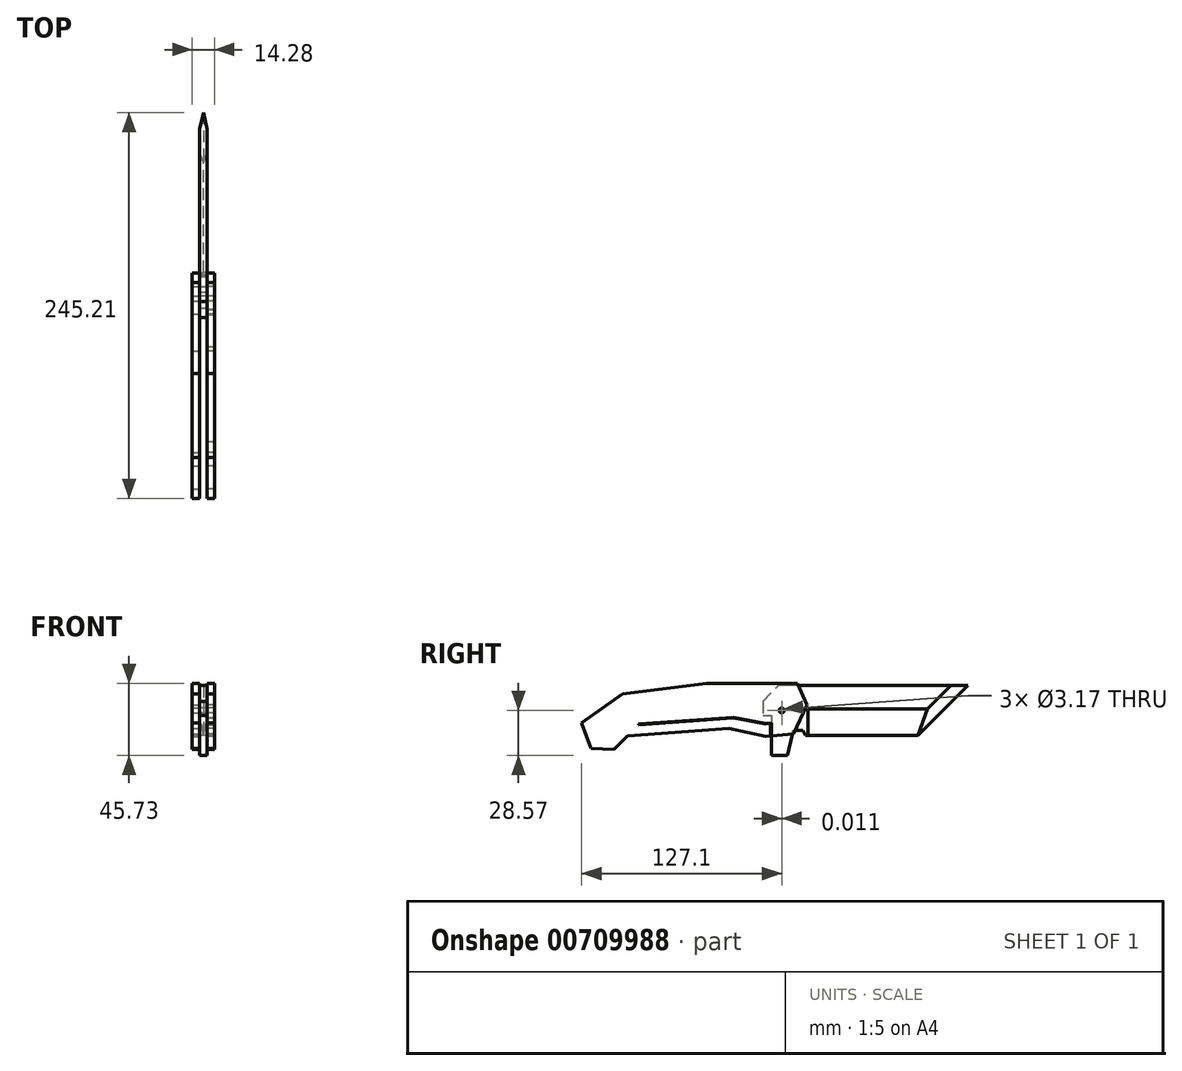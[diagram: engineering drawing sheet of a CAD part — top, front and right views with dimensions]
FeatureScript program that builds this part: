
annotation { "Feature Type Name" : "Feature", "Feature Type Description" : "" }
export const myFeature = defineFeature(function(context is Context, id is Id, definition is map)
    precondition{}
    {
        {
            var Q0;
            Q0=qCreatedBy(makeId("Right.planeOp"),FACE);
            var sketch = newSketch(context, id + "F0", { "sketchPlane" : qUnion([Q0])});
            skLineSegment(sketch, "E0.bottom", {"start": v(50.8, 15.88) * mm, "end": v(-50.8, 15.88) * mm});
            skLineSegment(sketch, "E0.top", {"start": v(50.8, -15.88) * mm, "end": v(-50.8, -15.88) * mm});
            skLineSegment(sketch, "E0.left", {"start": v(50.8, 15.88) * mm, "end": v(50.8, -15.88) * mm});
            skLineSegment(sketch, "E0.right", {"start": v(-50.8, 15.88) * mm, "end": v(-50.8, -15.88) * mm});
            skPoint(sketch, "E0.middle", {"position": v(0, 0) * mm});
            skSolve(sketch);
        }
        {
            var Q0;
            Q0 = qSketchRegion(id + "F0", true);
            extrude(context, id + "F1", {"entities" : qUnion([Q0]), "endBound" : BoundingType.SYMMETRIC, "oppositeDirection" : true, "depth" : 4.76 * mm, "offsetDistance" : 25.4 * mm});
        }
        {
            var Q0;
            Q0=makeQuery(id+"F1.opExtrude","SWEPT_FACE",FACE,{"disambiguationData":[OSD([sQuery(id+"F0.wireOp",EDGE,"E0.left")])]});
            var sketch = newSketch(context, id + "F2", { "sketchPlane" : qUnion([Q0])});
            skLineSegment(sketch, "E1", {"start": v(0, -15.87) * mm, "end": v(-2.38, 1.07) * mm});
            skLineSegment(sketch, "E2", {"start": v(0, -15.87) * mm, "end": v(0, -2.24) * mm, "construction": true});
            skLineSegment(sketch, "E3", {"start": v(0, -15.88) * mm, "end": v(2.38, 1.07) * mm});
            skLineSegment(sketch, "E4", {"start": v(-2.38, 1.07) * mm, "end": v(-18.49, 1.07) * mm});
            skLineSegment(sketch, "E5", {"start": v(-18.49, 1.07) * mm, "end": v(-18.49, -23.62) * mm});
            skLineSegment(sketch, "E6", {"start": v(-18.49, -23.62) * mm, "end": v(17.54, -23.62) * mm});
            skLineSegment(sketch, "E7", {"start": v(17.54, -23.62) * mm, "end": v(17.54, 1.07) * mm});
            skLineSegment(sketch, "E8", {"start": v(17.54, 1.07) * mm, "end": v(2.38, 1.07) * mm});
            skSolve(sketch);
        }
        {
            var Q0;
            Q0 = qSketchRegion(id + "F2", true);
            extrude(context, id + "F3", {"entities" : qUnion([Q0]), "operationType" : NewBodyOperationType.REMOVE, "endBound" : BoundingType.THROUGH_ALL, "oppositeDirection" : true, "depth" : 25.4 * mm, "offsetDistance" : 25.4 * mm});
        }
        {
            var Q0;
            Q0=qCreatedBy(makeId("Right.planeOp"),FACE);
            var sketch = newSketch(context, id + "F4", { "sketchPlane" : qUnion([Q0])});
            skLineSegment(sketch, "E9", {"start": v(50.8, 15.88) * mm, "end": v(19.05, -15.88) * mm});
            skSolve(sketch);
        }
        {
            var Q0;
            Q0=makeQuery(id+"F1.opExtrude","SWEPT_FACE",FACE,{"disambiguationData":[OSD([sQuery(id+"F0.wireOp",EDGE,"E0.bottom")])]});
            var sketch = newSketch(context, id + "F5", { "sketchPlane" : qUnion([Q0])});
            skLineSegment(sketch, "E10", {"start": v(0, 50.8) * mm, "end": v(2.38, 40.06) * mm});
            skLineSegment(sketch, "E11", {"start": v(0, 50.8) * mm, "end": v(-2.38, 40.06) * mm});
            skLineSegment(sketch, "E12", {"start": v(2.38, 40.06) * mm, "end": v(25.29, 40.06) * mm});
            skLineSegment(sketch, "E13", {"start": v(25.29, 40.06) * mm, "end": v(21.97, 103.42) * mm});
            skLineSegment(sketch, "E14", {"start": v(21.97, 103.42) * mm, "end": v(-23.8, 103.42) * mm});
            skLineSegment(sketch, "E15", {"start": v(-23.8, 103.42) * mm, "end": v(-27.67, 37.97) * mm});
            skLineSegment(sketch, "E16", {"start": v(-27.67, 37.97) * mm, "end": v(-2.38, 40.06) * mm});
            skSolve(sketch);
        }
        {
            var Q0;
            Q0 = qSketchRegion(id + "F5", true);
            var Q1;
            Q1 = qSketchRegion(id + "F4", true);
            var Q2;
            Q2 = qConstructionFilter(qBodyType(qCreatedBy(id + "F4" ,EDGE), BodyType.WIRE), ConstructionObject.NO);
            sweep(context, id + "F6", {"operationType" : NewBodyOperationType.REMOVE, "profiles" : qUnion([Q0, Q1]), "path" : qUnion([Q2])});
        }
        {
            var Q0;
            Q0=qCreatedBy(makeId("Right.planeOp"),FACE);
            var sketch = newSketch(context, id + "F7", { "sketchPlane" : qUnion([Q0])});
            skLineSegment(sketch, "E17", {"start": v(-50.8, -15.87) * mm, "end": v(-52.39, -15.87) * mm});
            skLineSegment(sketch, "E18", {"start": v(-50.8, 15.88) * mm, "end": v(-79.38, 15.87) * mm});
            skLineSegment(sketch, "E19", {"start": v(-79.38, 15.87) * mm, "end": v(-79.38, -3.17) * mm});
            skLineSegment(sketch, "E20", {"start": v(-79.38, -3.18) * mm, "end": v(-73.85, -3.18) * mm});
            skLineSegment(sketch, "E21", {"start": v(-73.85, -3.18) * mm, "end": v(-73.85, -28.58) * mm});
            skLineSegment(sketch, "E22", {"start": v(-73.85, -28.58) * mm, "end": v(-63.69, -28.58) * mm});
            skLineSegment(sketch, "E23", {"start": v(-63.69, -28.58) * mm, "end": v(-60.04, -12.7) * mm});
            skLineSegment(sketch, "E24", {"start": v(-60.04, -12.7) * mm, "end": v(-53.69, -12.7) * mm});
            skLineSegment(sketch, "E25", {"start": v(-53.69, -12.7) * mm, "end": v(-52.39, -15.87) * mm});
            skLineSegment(sketch, "E26", {"start": v(-50.8, 15.88) * mm, "end": v(-50.8, -15.87) * mm});
            skCircle(sketch, "E27", {"center": v(-67.31, 0) * mm, "radius": 1.59 * mm});
            skSolve(sketch);
        }
        {
            var Q0;
            Q0 = qSketchRegion(id + "F7", true);
            extrude(context, id + "F8", {"entities" : qUnion([Q0]), "operationType" : NewBodyOperationType.ADD, "endBound" : BoundingType.SYMMETRIC, "depth" : 4.76 * mm, "offsetDistance" : 25.4 * mm});
        }
        {
            var Q0;
            Q0=makeQuery(id+"F8.opExtrude","SWEPT_EDGE",EDGE,{"disambiguationData":[OSD([sQuery(id+"F7.wireOp",EDGE,"E18"),sQuery(id+"F7.wireOp",EDGE,"E19")])]});
            chamfer(context, id + "F9", {"entities" : qUnion([Q0]), "width" : 10.16 * mm, "tangentPropagation" : true});
        }
        {
            var Q0;
            Q0=makeQuery(id+"F8.boolean.opBoolean","MERGE",FACE,{"derivedFrom":[makeQuery(id+"F1.opExtrude","CAP_FACE",FACE,{"disambiguationData":[OSD([sQuery(id+"F0.wireOp",EDGE,"E0.bottom"),sQuery(id+"F0.wireOp",EDGE,"E0.top"),sQuery(id+"F0.wireOp",EDGE,"E0.left"),sQuery(id+"F0.wireOp",EDGE,"E0.right")])],"isStart":true}),makeQuery(id+"F8.opExtrude","CAP_FACE",FACE,{"disambiguationData":[OSD([sQuery(id+"F7.wireOp",EDGE,"E17"),sQuery(id+"F7.wireOp",EDGE,"E18"),sQuery(id+"F7.wireOp",EDGE,"E19"),sQuery(id+"F7.wireOp",EDGE,"E20"),sQuery(id+"F7.wireOp",EDGE,"E21"),sQuery(id+"F7.wireOp",EDGE,"E22"),sQuery(id+"F7.wireOp",EDGE,"E23"),sQuery(id+"F7.wireOp",EDGE,"E24"),sQuery(id+"F7.wireOp",EDGE,"E25"),sQuery(id+"F7.wireOp",EDGE,"E26"),sQuery(id+"F7.wireOp",EDGE,"E27")])],"isStart":false})]});
            var sketch = newSketch(context, id + "F10", { "sketchPlane" : qUnion([Q0])});
            skCircle(sketch, "E28", {"center": v(-67.31, 0) * mm, "radius": 15.88 * mm, "construction": true});
            skSolve(sketch);
        }
        {
            var Q0;
            {var subQ8=sQuery(id+"F7.wireOp",EDGE,"E17");Q0=makeQuery(id+"F10.imprint","IMPRINT",FACE,{"disambiguationData":[TD([[makeQuery(id+"F10.imprint","IMPRINT",EDGE,{"derivedFrom":makeQuery(id+"F8.opExtrude","CAP_EDGE",EDGE,{"disambiguationData":[OSD([subQ8])],"isStart":false})}),-1.0]])]});}
            var sketch = newSketch(context, id + "F11", { "sketchPlane" : qUnion([Q0])});
            skLineSegment(sketch, "E29", {"start": v(-115.05, 17.16) * mm, "end": v(-57.22, 17.16) * mm});
            skLineSegment(sketch, "E30", {"start": v(-57.22, 17.16) * mm, "end": v(-51.23, 3.41) * mm});
            skLineSegment(sketch, "E31", {"start": v(-51.23, 3.41) * mm, "end": v(-59.74, -14.96) * mm});
            skLineSegment(sketch, "E32", {"start": v(-59.74, -14.96) * mm, "end": v(-77.17, -16.54) * mm});
            skLineSegment(sketch, "E33", {"start": v(-77.17, -16.54) * mm, "end": v(-100.87, -11.45) * mm});
            skLineSegment(sketch, "E34", {"start": v(-100.87, -11.45) * mm, "end": v(-165.33, -16.07) * mm});
            skPoint(sketch, "E34.endSnap0", {"position": v(-89.02, -14) * mm});
            skLineSegment(sketch, "E35", {"start": v(-165.33, -16.07) * mm, "end": v(-173.7, -24.81) * mm});
            skLineSegment(sketch, "E36", {"start": v(-188.34, -24.23) * mm, "end": v(-173.7, -24.81) * mm});
            skLineSegment(sketch, "E37", {"start": v(-188.34, -24.23) * mm, "end": v(-194.41, -8) * mm});
            skLineSegment(sketch, "E38", {"start": v(-194.41, -8) * mm, "end": v(-168.37, 10.54) * mm});
            skLineSegment(sketch, "E39", {"start": v(-168.37, 10.54) * mm, "end": v(-115.05, 17.16) * mm});
            skCircle(sketch, "E40", {"center": v(-67.3, 0) * mm, "radius": 1.59 * mm});
            skSolve(sketch);
        }
        {
            var Q0;
            Q0 = qSketchRegion(id + "F11", true);
            extrude(context, id + "F12", {"entities" : qUnion([Q0]), "depth" : 4.76 * mm, "offsetDistance" : 25.4 * mm});
        }
        {
            var Q0;
            Q0=makeQuery(id+"F12.opExtrude","SWEPT_BODY",BODY,{"disambiguationData":[OSD([sQuery(id+"F11.wireOp",EDGE,"E29"),sQuery(id+"F11.wireOp",EDGE,"E30"),sQuery(id+"F11.wireOp",EDGE,"E31"),sQuery(id+"F11.wireOp",EDGE,"E32"),sQuery(id+"F11.wireOp",EDGE,"E33"),sQuery(id+"F11.wireOp",EDGE,"E34"),sQuery(id+"F11.wireOp",EDGE,"E35"),sQuery(id+"F11.wireOp",EDGE,"E36"),sQuery(id+"F11.wireOp",EDGE,"E37"),sQuery(id+"F11.wireOp",EDGE,"E38"),sQuery(id+"F11.wireOp",EDGE,"E39"),sQuery(id+"F11.wireOp",EDGE,"E40")])]});
            var Q1;
            Q1=qCreatedBy(makeId("Right.planeOp"),FACE);
            mirror(context, id + "F13", {"entities" : qUnion([Q0]), "mirrorPlane" : qUnion([Q1])});
        }
        {
            var Q0;
            Q0=makeQuery(id+"F12.opExtrude","CAP_FACE",FACE,{"disambiguationData":[OSD([sQuery(id+"F11.wireOp",EDGE,"E29"),sQuery(id+"F11.wireOp",EDGE,"E30"),sQuery(id+"F11.wireOp",EDGE,"E31"),sQuery(id+"F11.wireOp",EDGE,"E32"),sQuery(id+"F11.wireOp",EDGE,"E33"),sQuery(id+"F11.wireOp",EDGE,"E34"),sQuery(id+"F11.wireOp",EDGE,"E35"),sQuery(id+"F11.wireOp",EDGE,"E36"),sQuery(id+"F11.wireOp",EDGE,"E37"),sQuery(id+"F11.wireOp",EDGE,"E38"),sQuery(id+"F11.wireOp",EDGE,"E39"),sQuery(id+"F11.wireOp",EDGE,"E40")])],"isStart":false});
            var sketch = newSketch(context, id + "F14", { "sketchPlane" : qUnion([Q0])});
            skLineSegment(sketch, "E41", {"start": v(-74.5, -16.3) * mm, "end": v(-74.5, -8.36) * mm});
            skLineSegment(sketch, "E42", {"start": v(-98.06, -4.89) * mm, "end": v(-158.23, -9.2) * mm});
            skLineSegment(sketch, "E43.0", {"start": v(-98.03, -4.37) * mm, "end": v(-158.28, -8.7) * mm});
            skLineSegment(sketch, "E43.2", {"start": v(-73.98, -16.25) * mm, "end": v(-73.98, -7.8) * mm});
            skLineSegment(sketch, "E44", {"start": v(-158.23, -9.2) * mm, "end": v(-158.28, -8.7) * mm});
            skLineSegment(sketch, "E45", {"start": v(-74.5, -16.3) * mm, "end": v(-73.98, -16.25) * mm});
            skLineSegment(sketch, "E46", {"start": v(-98.06, -4.89) * mm, "end": v(-77.56, -8.64) * mm});
            skLineSegment(sketch, "E47", {"start": v(-77.56, -8.64) * mm, "end": v(-74.5, -8.36) * mm});
            skLineSegment(sketch, "E48.0", {"start": v(-77.53, -8.13) * mm, "end": v(-73.98, -7.8) * mm});
            skLineSegment(sketch, "E48.1", {"start": v(-98.03, -4.37) * mm, "end": v(-77.53, -8.13) * mm});
            skSolve(sketch);
        }
        {
            var Q0;
            Q0 = qSketchRegion(id + "F14", true);
            var Q1;
            Q1=makeQuery(id+"F1.opExtrude","SWEPT_BODY",BODY,{"disambiguationData":[OSD([sQuery(id+"F0.wireOp",EDGE,"E0.bottom"),sQuery(id+"F0.wireOp",EDGE,"E0.top"),sQuery(id+"F0.wireOp",EDGE,"E0.left"),sQuery(id+"F0.wireOp",EDGE,"E0.right")])]});
            extrude(context, id + "F15", {"entities" : qUnion([Q0]), "operationType" : NewBodyOperationType.REMOVE, "endBound" : BoundingType.UP_TO_NEXT, "oppositeDirection" : true, "depth" : 25.4 * mm, "endBoundEntityBody" : qUnion([Q1]), "offsetDistance" : 25.4 * mm});
        }
    });
